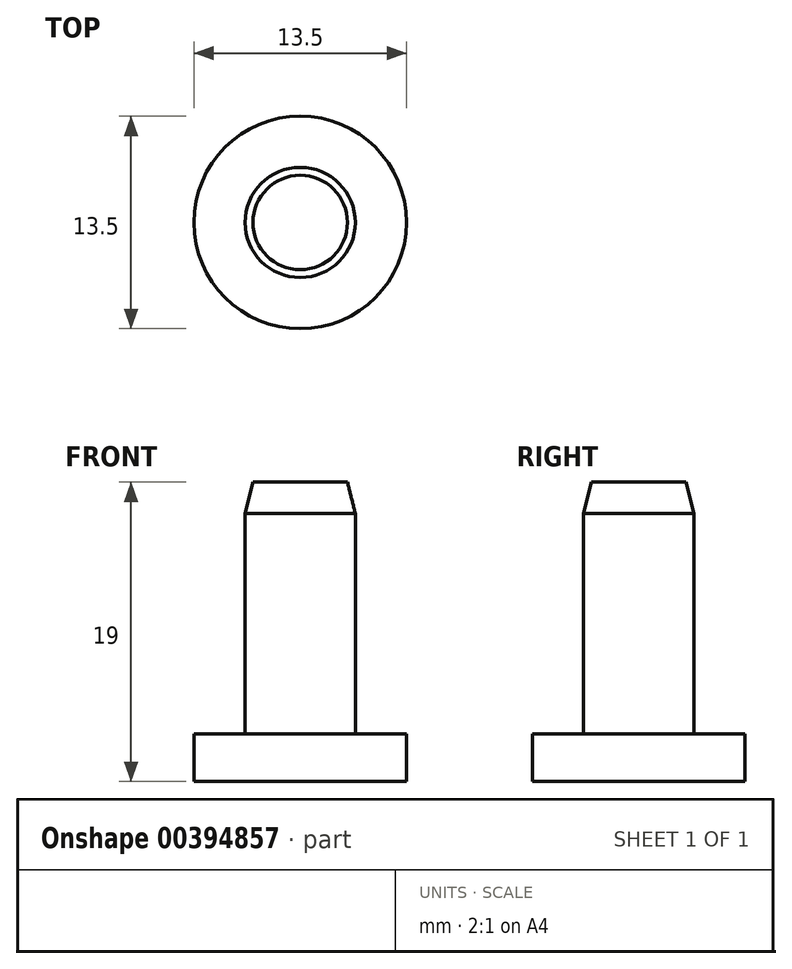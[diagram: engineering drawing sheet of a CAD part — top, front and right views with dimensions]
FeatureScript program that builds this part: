
annotation { "Feature Type Name" : "Feature", "Feature Type Description" : "" }
export const myFeature = defineFeature(function(context is Context, id is Id, definition is map)
    precondition{}
    {
        {
            var Q0;
            Q0=qCreatedBy(makeId("Front.planeOp"),FACE);
            var sketch = newSketch(context, id + "F0", { "sketchPlane" : qUnion([Q0])});
            skLineSegment(sketch, "E0", {"start": v(0, 0) * mm, "end": v(6.75, 0) * mm});
            skLineSegment(sketch, "E1", {"start": v(6.75, 0) * mm, "end": v(6.75, 3) * mm});
            skLineSegment(sketch, "E2", {"start": v(6.75, 3) * mm, "end": v(3.5, 3) * mm});
            skLineSegment(sketch, "E3", {"start": v(0, 0) * mm, "end": v(0, 29.18) * mm, "construction": true});
            skLineSegment(sketch, "E4", {"start": v(0, 19) * mm, "end": v(0, 0) * mm});
            skLineSegment(sketch, "E5", {"start": v(0, 19) * mm, "end": v(3, 19) * mm});
            skLineSegment(sketch, "E6", {"start": v(3, 19) * mm, "end": v(3.5, 17) * mm});
            skLineSegment(sketch, "E7", {"start": v(3.5, 17) * mm, "end": v(3.5, 3) * mm});
            skLineSegment(sketch, "E8", {"start": v(-10.98, 14) * mm, "end": v(16.07, 14) * mm, "construction": true});
            skLineSegment(sketch, "E9", {"start": v(-12.28, 8) * mm, "end": v(16.68, 8) * mm, "construction": true});
            skSolve(sketch);
        }
        {
            var Q0;
            Q0 = qSketchRegion(id + "F0", true);
            var Q1;
            Q1=sQuery(id+"F0.wireOp",EDGE,"E3");
            revolve(context, id + "F1", {"entities" : qUnion([Q0]), "axis" : qUnion([Q1]), "revolveType" : RevolveType.FULL, "oppositeDirection" : true});
        }
    });
